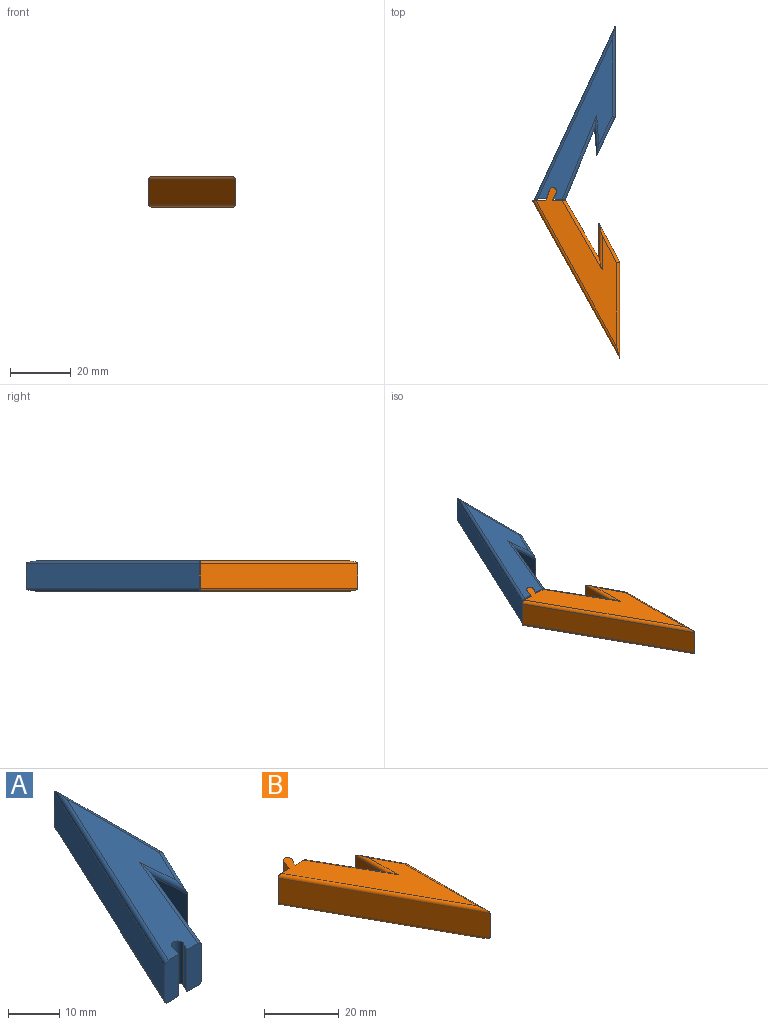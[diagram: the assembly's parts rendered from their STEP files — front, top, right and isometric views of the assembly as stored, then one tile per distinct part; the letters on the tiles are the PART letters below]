
ASSEMBLY  parts=2 mates=1
PART A: 22 faces, bbox 27.4x57.3x10 mm
  f0: plane 23.1x9.57mm, normal (0.92,-0.38,0), area 200mm2, adj f1,f9,f12,f17
  f1: plane 8.89x8mm, normal (-1,-0.08,0), area 71.3mm2, adj f0,f2,f13,f18
  f2: plane 12.64x8mm, normal (0.9,-0.43,0), area 112mm2, adj f1,f3,f14,f19
  f3: plane 30x8mm, normal (1,0,0), area 240mm2, adj f2,f4,f15,f20
  f4: plane 56.85x26.51mm, normal (-0.91,0.42,0), area 501.8mm2, adj f3,f5,f16,f21
  f5: plane 10x4.11mm, normal (0.04,-1,0), area 40.6mm2, adj f4,f6,f10,f11,f16,f21
  f6: plane 10x2.41mm, normal (0.96,-0.28,0), area 25.1mm2, adj f5,f7,f10,f11
  f7: cylinder r=1.25mm len=10mm, axis (0,0,-1), area 46.9mm2, adj f6,f8,f10,f11
  f8: plane 10x1.76mm, normal (-0.88,0.47,0), area 20mm2, adj f7,f9,f10,f11
  f9: plane 10x4.11mm, normal (0,-1,0), area 40.6mm2, adj f0,f8,f10,f11,f12,f17
  f10: plane 52.34x24.38mm, normal (0,0,1), area 361.2mm2, adj f5,f6,f7,f8,f9,f17,f18,f19
  f11: plane 52.34x24.38mm, normal (0,0,-1), area 361.2mm2, adj f5,f6,f7,f8,f9,f12,f13,f14
  f12: cylinder r=1mm len=27.71mm, axis (0.38,0.92,0), area 41.9mm2, adj f0,f9,f11,f13
  f13: cylinder r=1mm len=13.12mm, axis (0.08,-1,0), area 14.3mm2, adj f1,f11,f12,f14
  f14: cylinder r=1mm len=13.07mm, axis (0.43,0.9,0), area 19.7mm2, adj f2,f11,f13,f15
  f15: cylinder r=1mm len=30mm, axis (0,1,0), area 44.4mm2, adj f3,f11,f14,f16
  f16: cylinder r=1mm len=57.27mm, axis (-0.42,-0.91,0), area 95.7mm2, adj f4,f5,f11,f15
  f17: cylinder r=1mm len=27.71mm, axis (-0.38,-0.92,0), area 41.9mm2, adj f0,f9,f10,f18
  f18: cylinder r=1mm len=13.12mm, axis (-0.08,1,0), area 14.3mm2, adj f1,f10,f17,f19
  f19: cylinder r=1mm len=13.07mm, axis (-0.43,-0.9,0), area 19.7mm2, adj f2,f10,f18,f20
  f20: cylinder r=1mm len=30mm, axis (0,-1,0), area 44.4mm2, adj f3,f10,f19,f21
  f21: cylinder r=1mm len=57.27mm, axis (0.42,0.91,0), area 95.7mm2, adj f4,f5,f10,f20
PART B: 22 faces, bbox 29.5x55.9x10 mm
  f0: plane 10x4.45mm, normal (0,1,0), area 44mm2, adj f6,f7,f8,f12,f17,f21
  f1: plane 10x4.45mm, normal (0,1,0), area 44mm2, adj f2,f7,f8,f9,f14,f20
  f2: plane 51.68x28.61mm, normal (-0.87,-0.48,0), area 472.6mm2, adj f1,f3,f9,f14
  f3: plane 31.5x8mm, normal (1,0,0), area 252mm2, adj f2,f4,f10,f15
  f4: plane 12.71x8mm, normal (0.88,0.47,0), area 115.2mm2, adj f3,f5,f11,f16
  f5: plane 11.5x8mm, normal (-1,0,0), area 92mm2, adj f4,f6,f13,f18
  f6: plane 18.97x10.95mm, normal (0.87,0.5,0), area 175.2mm2, adj f0,f5,f12,f17
  f7: plane 52.05x26.47mm, normal (0,0,1), area 417.5mm2, adj f0,f1,f9,f10,f11,f12,f13,f19
  f8: plane 52.05x26.47mm, normal (0,0,-1), area 417.5mm2, adj f0,f1,f14,f15,f16,f17,f18,f19
  f9: cylinder r=1mm len=52.16mm, axis (-0.48,0.87,0), area 90.3mm2, adj f1,f2,f7,f10
  f10: cylinder r=1mm len=31.5mm, axis (0,-1,0), area 47.1mm2, adj f3,f7,f9,f11
  f11: cylinder r=1mm len=13.18mm, axis (0.47,-0.88,0), area 20.2mm2, adj f4,f7,f10,f13
  f12: cylinder r=1mm len=23.2mm, axis (0.5,-0.87,0), area 36.9mm2, adj f0,f6,f7,f13
  f13: cylinder r=1mm len=15.23mm, axis (0,1,0), area 17.9mm2, adj f5,f7,f11,f12
  f14: cylinder r=1mm len=52.16mm, axis (0.48,-0.87,0), area 90.3mm2, adj f1,f2,f8,f15
  f15: cylinder r=1mm len=31.5mm, axis (0,1,0), area 47.1mm2, adj f3,f8,f14,f16
  f16: cylinder r=1mm len=13.18mm, axis (-0.47,0.88,0), area 20.2mm2, adj f4,f8,f15,f18
  f17: cylinder r=1mm len=23.2mm, axis (-0.5,0.87,0), area 36.9mm2, adj f0,f6,f8,f18
  f18: cylinder r=1mm len=15.23mm, axis (0,-1,0), area 17.9mm2, adj f5,f8,f16,f17
  f19: cylinder r=1.25mm len=10mm, axis (0,0,-1), area 40.4mm2, adj f7,f8,f20,f21
  f20: plane 10x3.36mm, normal (-0.95,0.3,0), area 35.2mm2, adj f1,f7,f8,f19
  f21: plane 10x2.51mm, normal (0.87,-0.49,0), area 28.7mm2, adj f0,f7,f8,f19
PLACE A t=(23.51,0,36.42)mm
PLACE B t=(41.28,-52.15,36.42)mm
MATE slider B.f19 <-> A.f7  axis (0,0,-1) through (19.36,2.52,41.42)mm
